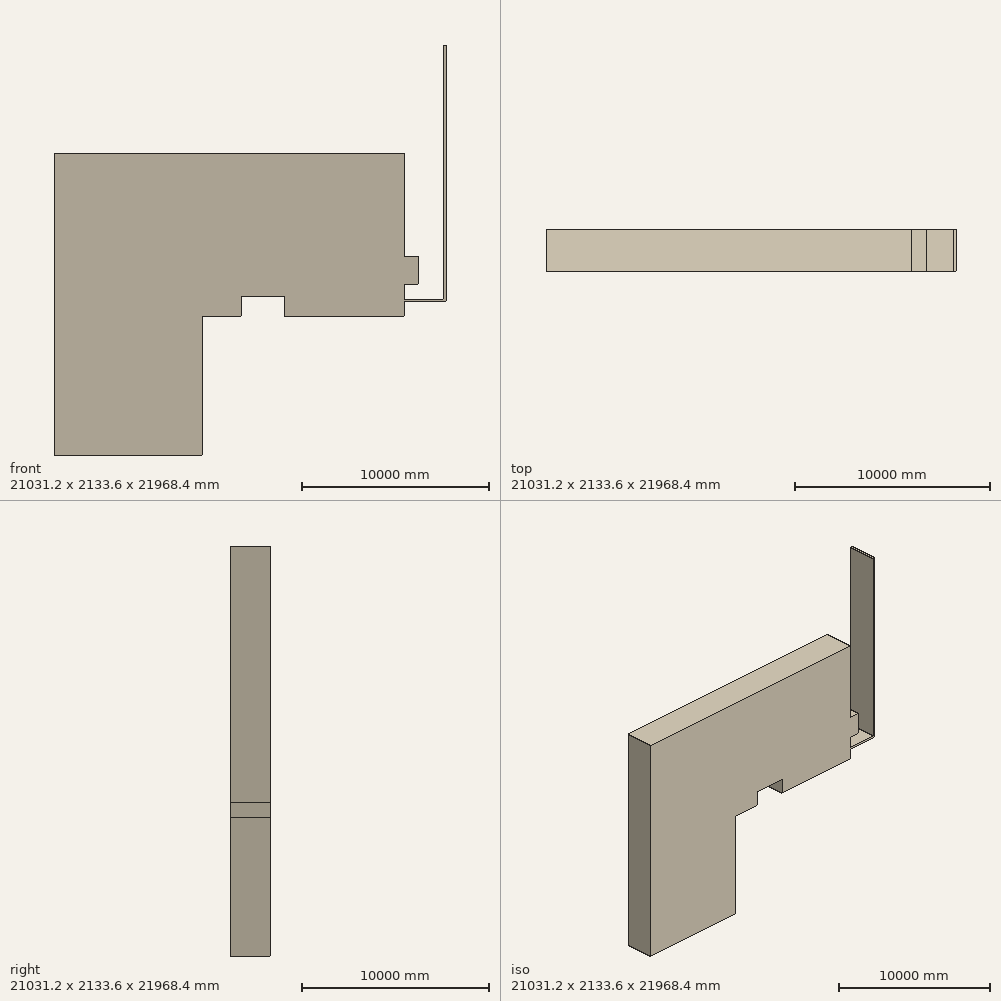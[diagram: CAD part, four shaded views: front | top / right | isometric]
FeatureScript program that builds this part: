
annotation { "Feature Type Name" : "Feature", "Feature Type Description" : "" }
export const myFeature = defineFeature(function(context is Context, id is Id, definition is map)
    precondition{}
    {
        {
            var Q0;
            Q0=qCreatedBy(makeId("Front.planeOp"),FACE);
            var sketch = newSketch(context, id + "F0", { "sketchPlane" : qUnion([Q0])});
            skLineSegment(sketch, "E0", {"start": v(0, 0) * mm, "end": v(7924.8, 0) * mm});
            skLineSegment(sketch, "E1", {"start": v(7924.8, 0) * mm, "end": v(7924.8, 7467.6) * mm});
            skLineSegment(sketch, "E2", {"start": v(7924.8, 7467.6) * mm, "end": v(10058.4, 7467.6) * mm});
            skLineSegment(sketch, "E3", {"start": v(10058.4, 7467.6) * mm, "end": v(10058.4, 8534.4) * mm});
            skLineSegment(sketch, "E4", {"start": v(10058.4, 8534.4) * mm, "end": v(12344.4, 8534.4) * mm});
            skLineSegment(sketch, "E5", {"start": v(12344.4, 8534.4) * mm, "end": v(12344.4, 7467.6) * mm});
            skLineSegment(sketch, "E6", {"start": v(12344.4, 7467.6) * mm, "end": v(18745.2, 7467.6) * mm});
            skLineSegment(sketch, "E7", {"start": v(18745.2, 7467.6) * mm, "end": v(18745.2, 8229.6) * mm});
            skLineSegment(sketch, "E8", {"start": v(18745.2, 16154.4) * mm, "end": v(0, 16154.4) * mm});
            skLineSegment(sketch, "E9", {"start": v(0, 16154.4) * mm, "end": v(0, 0) * mm});
            skLineSegment(sketch, "E10", {"start": v(18745.2, 8229.6) * mm, "end": v(21031.2, 8229.6) * mm});
            skLineSegment(sketch, "E11", {"start": v(20878.8, 8382) * mm, "end": v(18745.2, 8382) * mm});
            skLineSegment(sketch, "E12.trimOffspring", {"start": v(18745.2, 8382) * mm, "end": v(18745.2, 9144) * mm});
            skLineSegment(sketch, "E13.bottom", {"start": v(18745.2, 9144) * mm, "end": v(19507.2, 9144) * mm});
            skLineSegment(sketch, "E13.top", {"start": v(18745.2, 10668) * mm, "end": v(19507.2, 10668) * mm});
            skLineSegment(sketch, "E13.right", {"start": v(19507.2, 9144) * mm, "end": v(19507.2, 10668) * mm});
            skLineSegment(sketch, "E14.trimOffspring", {"start": v(18745.2, 10668) * mm, "end": v(18745.2, 16154.4) * mm});
            skLineSegment(sketch, "E15.top", {"start": v(20878.8, 21968.44) * mm, "end": v(21031.2, 21968.44) * mm});
            skLineSegment(sketch, "E15.left", {"start": v(20878.8, 8382) * mm, "end": v(20878.8, 21968.44) * mm});
            skLineSegment(sketch, "E15.right", {"start": v(21031.2, 8229.6) * mm, "end": v(21031.2, 21968.44) * mm});
            skSolve(sketch);
        }
        {
            var Q0;
            Q0=makeQuery(id+"F0.imprint","IMPRINT",FACE,{"disambiguationData":[TD([[makeQuery(id+"F0.imprint","IMPRINT",EDGE,{"derivedFrom":sQuery(id+"F0.wireOp",EDGE,"E0")}),1.0]])]});
            extrude(context, id + "F1", {"entities" : qUnion([Q0]), "oppositeDirection" : true, "depth" : 2133.6 * mm, "offsetDistance" : 30.48 * mm});
        }
    });
